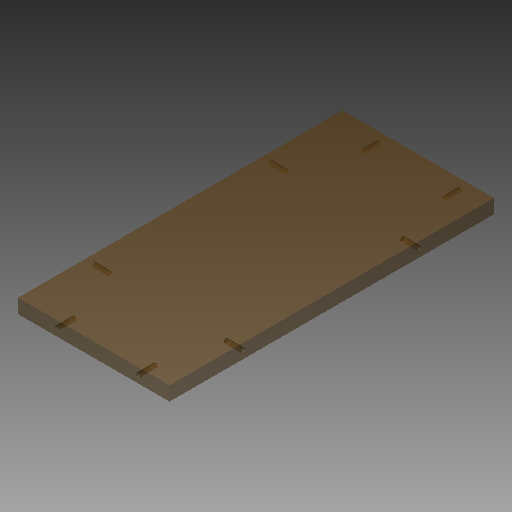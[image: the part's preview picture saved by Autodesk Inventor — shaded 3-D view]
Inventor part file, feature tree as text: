
AUTODESK INVENTOR PART (.ipt)
format: ipt  version: 2018 (Build 220112000, 112)  size: 108,032 bytes
history: native  units: mm
features: reference x4, hole x3, extrude x1, mirror x1
ambient origin geometry x8: Origin, YZ Plane, XZ Plane, XY Plane, X Axis, Y Axis, Z Axis, Center Point
bodies: Volumenkörper1 (feature_tree)
feature tree (9):
  extrude  "Extrusion1"  Depth=184.0mm
  hole  "Bohrung1"  [1 undecoded]
  hole  "Bohrung2"  [1 undecoded]
  mirror  "Spiegeln1"
  hole  "Bohrung3"  [1 undecoded]
  reference  "Referenz1"
  reference  "Referenz2"
  reference  "Referenz3"
  reference  "Referenz4"
note: 3 required parameter values undecoded (feature->parameter linkage not recoverable at this tier; creation-order binding heuristic only, values carry confidence <= 0.55)
